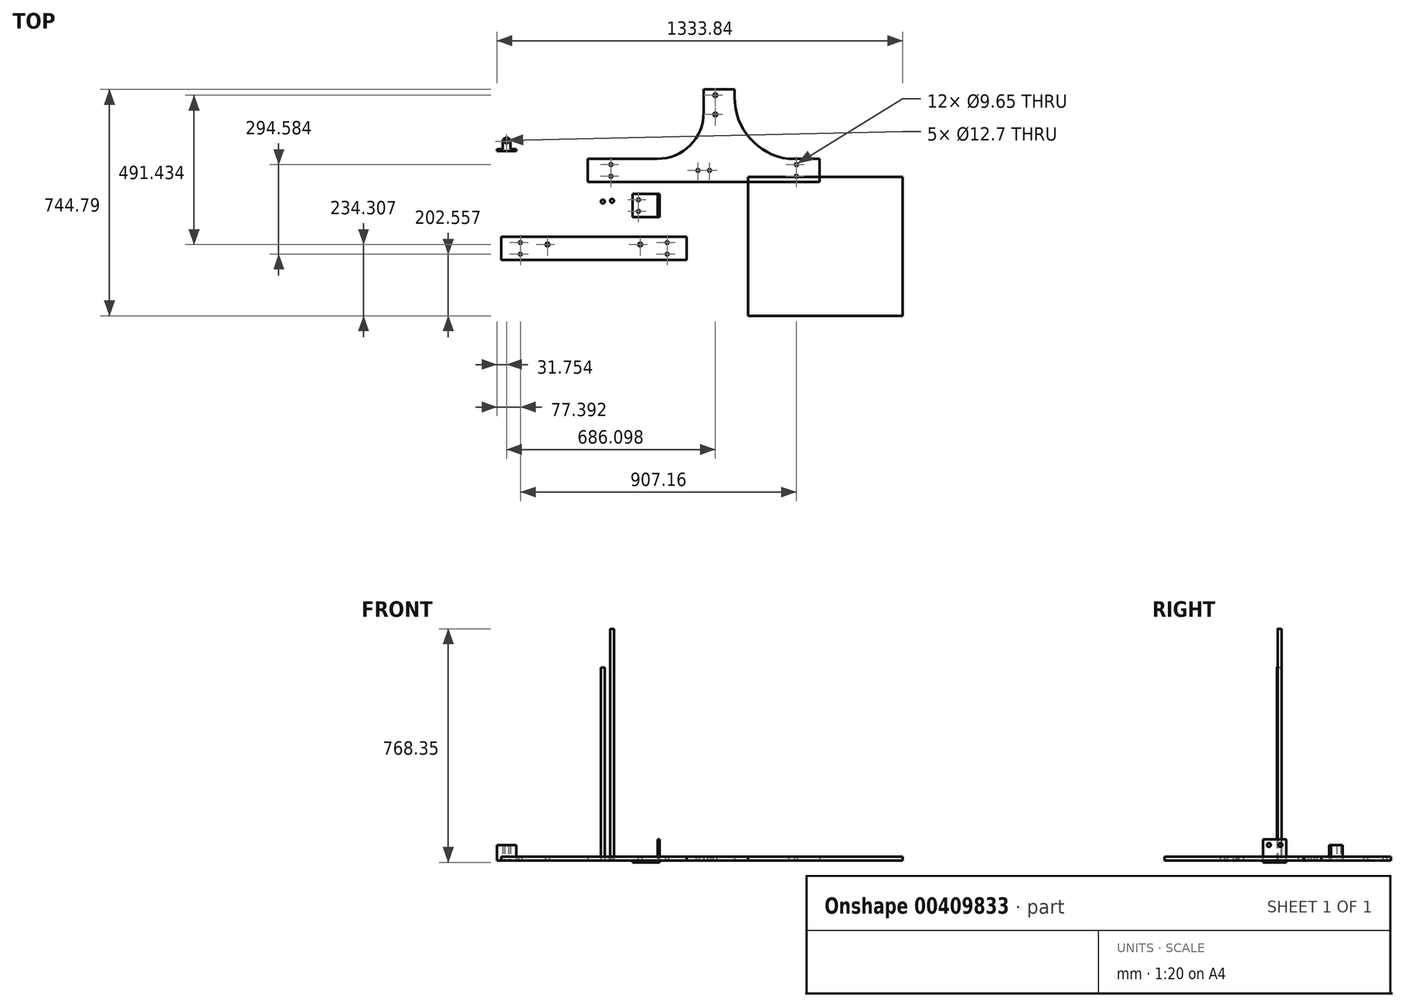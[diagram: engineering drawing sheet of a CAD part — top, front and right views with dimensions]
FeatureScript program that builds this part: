
annotation { "Feature Type Name" : "Feature", "Feature Type Description" : "" }
export const myFeature = defineFeature(function(context is Context, id is Id, definition is map)
    precondition{}
    {
        {
            var Q0;
            Q0=qCreatedBy(makeId("Top.planeOp"),FACE);
            var sketch = newSketch(context, id + "F0", { "sketchPlane" : qUnion([Q0])});
            skLineSegment(sketch, "E0.bottom", {"start": v(-396.76, -185.12) * mm, "end": v(212.84, -185.12) * mm});
            skLineSegment(sketch, "E0.top", {"start": v(-396.76, -261.32) * mm, "end": v(212.84, -261.32) * mm});
            skLineSegment(sketch, "E0.left", {"start": v(-396.76, -185.12) * mm, "end": v(-396.76, -261.32) * mm});
            skLineSegment(sketch, "E0.right", {"start": v(212.84, -185.12) * mm, "end": v(212.84, -261.32) * mm});
            skSolve(sketch);
        }
        {
            var Q0;
            Q0=makeQuery(id+"F0.imprint","IMPRINT",FACE,{"disambiguationData":[TD([[makeQuery(id+"F0.imprint","IMPRINT",EDGE,{"derivedFrom":sQuery(id+"F0.wireOp",EDGE,"E0.bottom")}),-1.0]])]});
            extrude(context, id + "F1", {"entities" : qUnion([Q0]), "depth" : 12.7 * mm});
        }
        {
            var Q0;
            Q0=qCreatedBy(makeId("Top.planeOp"),FACE);
            var sketch = newSketch(context, id + "F2", { "sketchPlane" : qUnion([Q0])});
            skLineSegment(sketch, "E1.bottom", {"start": v(-111.9, 71.36) * mm, "end": v(116.7, 71.36) * mm});
            skLineSegment(sketch, "E1.top", {"start": v(-111.9, -4.84) * mm, "end": v(650.1, -4.84) * mm});
            skLineSegment(sketch, "E1.left", {"start": v(-111.9, 71.36) * mm, "end": v(-111.9, -4.84) * mm});
            skLineSegment(sketch, "E1.right", {"start": v(650.1, 71.36) * mm, "end": v(650.1, -4.84) * mm});
            skLineSegment(sketch, "E2.top", {"start": v(269.1, 299.96) * mm, "end": v(370.7, 299.96) * mm});
            skLineSegment(sketch, "E2.left", {"start": v(269.1, 223.76) * mm, "end": v(269.1, 299.96) * mm});
            skLineSegment(sketch, "E2.right", {"start": v(370.7, 274.56) * mm, "end": v(370.7, 299.96) * mm});
            skLineSegment(sketch, "E3.trimOffspring", {"start": v(548.5, 71.36) * mm, "end": v(650.1, 71.36) * mm});
            skArc(sketch, "E4", {"start": v(116.7, 71.36) * mm, "mid": v(224.47, 116) * mm, "end": v(269.1, 223.76) * mm});
            skArc(sketch, "E5", {"start": v(370.7, 274.56) * mm, "mid": v(420.97, 139.16) * mm, "end": v(548.5, 71.36) * mm});
            skPoint(sketch, "E6.orphan", {"position": v(269.1, 71.36) * mm});
            skSolve(sketch);
        }
        {
            var Q0;
            Q0=makeQuery(id+"F2.imprint","IMPRINT",FACE,{"disambiguationData":[TD([[makeQuery(id+"F2.imprint","IMPRINT",EDGE,{"derivedFrom":sQuery(id+"F2.wireOp",EDGE,"E1.bottom")}),-1.0]])]});
            extrude(context, id + "F3", {"entities" : qUnion([Q0]), "depth" : 12.7 * mm});
        }
        {
            var Q0;
            Q0=makeQuery(id+"F1.opExtrude","CAP_FACE",FACE,{"disambiguationData":[OSD([sQuery(id+"F0.wireOp",EDGE,"E0.bottom"),sQuery(id+"F0.wireOp",EDGE,"E0.top"),sQuery(id+"F0.wireOp",EDGE,"E0.left"),sQuery(id+"F0.wireOp",EDGE,"E0.right")])],"isStart":false});
            var sketch = newSketch(context, id + "F4", { "sketchPlane" : qUnion([Q0])});
            skLineSegment(sketch, "E7", {"start": v(212.84, -223.22) * mm, "end": v(149.34, -223.22) * mm});
            skLineSegment(sketch, "E8", {"start": v(149.34, -223.22) * mm, "end": v(149.34, -204.17) * mm});
            skLineSegment(sketch, "E9.1.0.0", {"start": v(187.44, -223.22) * mm, "end": v(187.44, -204.17) * mm});
            skLineSegment(sketch, "E9.direction1", {"start": v(149.34, -223.22) * mm, "end": v(187.44, -223.22) * mm, "construction": true});
            skLineSegment(sketch, "E10.MirrorCS", {"start": v(187.44, -223.22) * mm, "end": v(187.44, -242.27) * mm});
            skLineSegment(sketch, "E11.MirrorCS", {"start": v(149.34, -223.22) * mm, "end": v(149.34, -242.27) * mm});
            skPoint(sketch, "E12.end.orphan", {"position": v(-91.96, -261.32) * mm});
            skPoint(sketch, "E12.start.orphan", {"position": v(-91.96, -185.12) * mm});
            skLineSegment(sketch, "E13", {"start": v(-91.96, -261.32) * mm, "end": v(-91.96, -241.2) * mm});
            skLineSegment(sketch, "E14.MirrorCS", {"start": v(-333.26, -223.22) * mm, "end": v(-333.26, -242.27) * mm});
            skLineSegment(sketch, "E15.MirrorCS", {"start": v(-371.36, -223.22) * mm, "end": v(-371.36, -242.27) * mm});
            skLineSegment(sketch, "E16.MirrorCS", {"start": v(-371.36, -223.22) * mm, "end": v(-371.36, -204.17) * mm});
            skLineSegment(sketch, "E17.MirrorCS", {"start": v(-333.26, -223.22) * mm, "end": v(-333.26, -204.17) * mm});
            skLineSegment(sketch, "E18", {"start": v(-91.96, -185.12) * mm, "end": v(-244.36, -185.12) * mm});
            skLineSegment(sketch, "E19", {"start": v(-91.96, -185.12) * mm, "end": v(60.44, -185.12) * mm});
            skLineSegment(sketch, "E20", {"start": v(-244.36, -185.12) * mm, "end": v(-244.36, -210.52) * mm});
            skLineSegment(sketch, "E21", {"start": v(60.44, -185.12) * mm, "end": v(60.44, -210.52) * mm});
            skSolve(sketch);
        }
        {
            var Q0;
            Q0=sQuery(id+"F4.wireOp",VERTEX,"E11.MirrorCS.end");
            var Q1;
            Q1=sQuery(id+"F4.wireOp",VERTEX,"E8.end");
            var Q2;
            Q2=sQuery(id+"F4.wireOp",VERTEX,"9953c66d-f5c9-40e7-a042-aea70b481f3b0.MirrorCS.end");
            var Q3;
            Q3=sQuery(id+"F4.wireOp",VERTEX,"f008637d-56cd-4cf4-9467-72500eb1184e0.MirrorCS.end");
            var Q4;
            Q4=sQuery(id+"F4.wireOp",VERTEX,"bad4df71-79ab-45ec-aa86-1bffc069c0d70.MirrorCS.end");
            var Q5;
            Q5=sQuery(id+"F4.wireOp",VERTEX,"125a2959-b819-4b87-9607-182dddcc34e20.MirrorCS.end");
            var Q6;
            Q6=makeQuery(id+"F1.opExtrude","SWEPT_BODY",BODY,{"disambiguationData":[OSD([sQuery(id+"F0.wireOp",EDGE,"E0.bottom"),sQuery(id+"F0.wireOp",EDGE,"E0.top"),sQuery(id+"F0.wireOp",EDGE,"E0.left"),sQuery(id+"F0.wireOp",EDGE,"E0.right")])]});
            hole(context, id + "F5", {"style" : HoleStyle.SIMPLE, "endStyle" : HoleEndStyle.BLIND, "holeDiameter" : 9.65 * mm, "holeDepth" : 25.4 * mm, "isTappedThrough" : true, "tappedDepth" : 12.7 * mm, "tapClearance" : 3, "locations" : qUnion([Q0, Q1, Q2, Q3, Q4, Q5]), "scope" : qUnion([Q6])});
        }
        {
            var Q0;
            Q0=makeQuery(id+"F3.opExtrude","CAP_FACE",FACE,{"disambiguationData":[OSD([sQuery(id+"F2.wireOp",EDGE,"E1.bottom"),sQuery(id+"F2.wireOp",EDGE,"E1.top"),sQuery(id+"F2.wireOp",EDGE,"E1.left"),sQuery(id+"F2.wireOp",EDGE,"E1.right"),sQuery(id+"F2.wireOp",EDGE,"E2.top"),sQuery(id+"F2.wireOp",EDGE,"E2.left"),sQuery(id+"F2.wireOp",EDGE,"E2.right"),sQuery(id+"F2.wireOp",EDGE,"E3.trimOffspring"),sQuery(id+"F2.wireOp",EDGE,"E4"),sQuery(id+"F2.wireOp",EDGE,"E5")])],"isStart":false});
            var sketch = newSketch(context, id + "F6", { "sketchPlane" : qUnion([Q0])});
            skLineSegment(sketch, "E22", {"start": v(-111.9, 33.26) * mm, "end": v(-35.7, 33.26) * mm});
            skLineSegment(sketch, "E23", {"start": v(-35.7, 33.26) * mm, "end": v(-35.7, 14.21) * mm});
            skLineSegment(sketch, "E24", {"start": v(-35.7, 14.21) * mm, "end": v(-73.8, 14.21) * mm});
            skLineSegment(sketch, "E25.MirrorCS", {"start": v(-35.7, 52.31) * mm, "end": v(-73.8, 52.31) * mm});
            skLineSegment(sketch, "E26", {"start": v(269.1, -4.84) * mm, "end": v(269.1, 15.48) * mm});
            skLineSegment(sketch, "E27.MirrorCS", {"start": v(573.9, 14.21) * mm, "end": v(612, 14.21) * mm});
            skLineSegment(sketch, "E28.MirrorCS", {"start": v(573.9, 52.31) * mm, "end": v(612, 52.31) * mm});
            skSolve(sketch);
        }
        {
            var Q0;
            Q0=sQuery(id+"F6.wireOp",VERTEX,"E25.MirrorCS.start");
            var Q1;
            Q1=sQuery(id+"F6.wireOp",VERTEX,"E24.start");
            var Q2;
            Q2=sQuery(id+"F6.wireOp",VERTEX,"E28.MirrorCS.start");
            var Q3;
            Q3=sQuery(id+"F6.wireOp",VERTEX,"E27.MirrorCS.start");
            var Q4;
            Q4=makeQuery(id+"F3.opExtrude","SWEPT_BODY",BODY,{"disambiguationData":[OSD([sQuery(id+"F2.wireOp",EDGE,"E1.bottom"),sQuery(id+"F2.wireOp",EDGE,"E1.top"),sQuery(id+"F2.wireOp",EDGE,"E1.left"),sQuery(id+"F2.wireOp",EDGE,"E1.right"),sQuery(id+"F2.wireOp",EDGE,"E2.top"),sQuery(id+"F2.wireOp",EDGE,"E2.left"),sQuery(id+"F2.wireOp",EDGE,"E2.right"),sQuery(id+"F2.wireOp",EDGE,"E3.trimOffspring"),sQuery(id+"F2.wireOp",EDGE,"E4"),sQuery(id+"F2.wireOp",EDGE,"E5")])]});
            hole(context, id + "F7", {"style" : HoleStyle.SIMPLE, "endStyle" : HoleEndStyle.BLIND, "holeDiameter" : 9.65 * mm, "holeDepth" : 25.4 * mm, "isTappedThrough" : true, "tappedDepth" : 12.7 * mm, "tapClearance" : 3, "locations" : qUnion([Q0, Q1, Q2, Q3]), "scope" : qUnion([Q4])});
        }
        {
            var Q0;
            Q0=sQuery(id+"F4.wireOp",VERTEX,"E17.MirrorCS.end");
            var Q1;
            Q1=sQuery(id+"F4.wireOp",VERTEX,"E14.MirrorCS.end");
            var Q2;
            Q2=makeQuery(id+"F1.opExtrude","SWEPT_BODY",BODY,{"disambiguationData":[OSD([sQuery(id+"F0.wireOp",EDGE,"E0.bottom"),sQuery(id+"F0.wireOp",EDGE,"E0.top"),sQuery(id+"F0.wireOp",EDGE,"E0.left"),sQuery(id+"F0.wireOp",EDGE,"E0.right")])]});
            hole(context, id + "F8", {"style" : HoleStyle.SIMPLE, "endStyle" : HoleEndStyle.BLIND, "holeDiameter" : 9.65 * mm, "holeDepth" : 25.4 * mm, "isTappedThrough" : true, "tappedDepth" : 12.7 * mm, "tapClearance" : 3, "locations" : qUnion([Q0, Q1]), "scope" : qUnion([Q2])});
        }
        {
            var Q0;
            Q0=makeQuery(id+"F3.opExtrude","CAP_FACE",FACE,{"disambiguationData":[OSD([sQuery(id+"F2.wireOp",EDGE,"E1.bottom"),sQuery(id+"F2.wireOp",EDGE,"E1.top"),sQuery(id+"F2.wireOp",EDGE,"E1.left"),sQuery(id+"F2.wireOp",EDGE,"E1.right"),sQuery(id+"F2.wireOp",EDGE,"E2.top"),sQuery(id+"F2.wireOp",EDGE,"E2.left"),sQuery(id+"F2.wireOp",EDGE,"E2.right"),sQuery(id+"F2.wireOp",EDGE,"E3.trimOffspring"),sQuery(id+"F2.wireOp",EDGE,"E4"),sQuery(id+"F2.wireOp",EDGE,"E5")])],"isStart":false});
            var sketch = newSketch(context, id + "F9", { "sketchPlane" : qUnion([Q0])});
            skLineSegment(sketch, "E29", {"start": v(269.1, -4.84) * mm, "end": v(269.1, 33.26) * mm});
            skLineSegment(sketch, "E30", {"start": v(269.1, 33.26) * mm, "end": v(288.15, 33.26) * mm});
            skLineSegment(sketch, "E31", {"start": v(269.1, 33.26) * mm, "end": v(250.05, 33.26) * mm});
            skSolve(sketch);
        }
        {
            var Q0;
            Q0=sQuery(id+"F9.wireOp",VERTEX,"E30.end");
            var Q1;
            Q1=sQuery(id+"F9.wireOp",VERTEX,"E31.end");
            var Q2;
            Q2=makeQuery(id+"F3.opExtrude","SWEPT_BODY",BODY,{"disambiguationData":[OSD([sQuery(id+"F2.wireOp",EDGE,"E1.bottom"),sQuery(id+"F2.wireOp",EDGE,"E1.top"),sQuery(id+"F2.wireOp",EDGE,"E1.left"),sQuery(id+"F2.wireOp",EDGE,"E1.right"),sQuery(id+"F2.wireOp",EDGE,"E2.top"),sQuery(id+"F2.wireOp",EDGE,"E2.left"),sQuery(id+"F2.wireOp",EDGE,"E2.right"),sQuery(id+"F2.wireOp",EDGE,"E3.trimOffspring"),sQuery(id+"F2.wireOp",EDGE,"E4"),sQuery(id+"F2.wireOp",EDGE,"E5")])]});
            hole(context, id + "F10", {"style" : HoleStyle.SIMPLE, "endStyle" : HoleEndStyle.BLIND, "holeDiameter" : 9.65 * mm, "holeDepth" : 25.4 * mm, "isTappedThrough" : true, "tappedDepth" : 12.7 * mm, "tapClearance" : 3, "locations" : qUnion([Q0, Q1]), "scope" : qUnion([Q2])});
        }
        {
            var Q0;
            Q0=makeQuery(id+"F3.opExtrude","CAP_FACE",FACE,{"disambiguationData":[OSD([sQuery(id+"F2.wireOp",EDGE,"E1.bottom"),sQuery(id+"F2.wireOp",EDGE,"E1.top"),sQuery(id+"F2.wireOp",EDGE,"E1.left"),sQuery(id+"F2.wireOp",EDGE,"E1.right"),sQuery(id+"F2.wireOp",EDGE,"E2.top"),sQuery(id+"F2.wireOp",EDGE,"E2.left"),sQuery(id+"F2.wireOp",EDGE,"E2.right"),sQuery(id+"F2.wireOp",EDGE,"E3.trimOffspring"),sQuery(id+"F2.wireOp",EDGE,"E4"),sQuery(id+"F2.wireOp",EDGE,"E5")])],"isStart":false});
            var sketch = newSketch(context, id + "F11", { "sketchPlane" : qUnion([Q0])});
            skLineSegment(sketch, "E32", {"start": v(307.2, 280.91) * mm, "end": v(307.2, 217.41) * mm});
            skPoint(sketch, "E33.start.orphan", {"position": v(319.9, 299.96) * mm});
            skSolve(sketch);
        }
        {
            var Q0;
            Q0=sQuery(id+"F11.wireOp",VERTEX,"E33.end");
            var Q1;
            Q1=sQuery(id+"F11.wireOp",VERTEX,"E32.end");
            var Q2;
            Q2=makeQuery(id+"F3.opExtrude","SWEPT_BODY",BODY,{"disambiguationData":[OSD([sQuery(id+"F2.wireOp",EDGE,"E1.bottom"),sQuery(id+"F2.wireOp",EDGE,"E1.top"),sQuery(id+"F2.wireOp",EDGE,"E1.left"),sQuery(id+"F2.wireOp",EDGE,"E1.right"),sQuery(id+"F2.wireOp",EDGE,"E2.top"),sQuery(id+"F2.wireOp",EDGE,"E2.left"),sQuery(id+"F2.wireOp",EDGE,"E2.right"),sQuery(id+"F2.wireOp",EDGE,"E3.trimOffspring"),sQuery(id+"F2.wireOp",EDGE,"E4"),sQuery(id+"F2.wireOp",EDGE,"E5")])]});
            hole(context, id + "F12", {"style" : HoleStyle.SIMPLE, "endStyle" : HoleEndStyle.BLIND, "holeDiameter" : 12.7 * mm, "holeDepth" : 25.4 * mm, "isTappedThrough" : true, "tappedDepth" : 12.7 * mm, "tapClearance" : 3, "locations" : qUnion([Q0, Q1]), "scope" : qUnion([Q2])});
        }
        {
            var Q0;
            Q0=qCreatedBy(makeId("Top.planeOp"),FACE);
            var sketch = newSketch(context, id + "F13", { "sketchPlane" : qUnion([Q0])});
            skCircle(sketch, "E34", {"center": v(-62.58, -69.02) * mm, "radius": 6.35 * mm});
            skSolve(sketch);
        }
        {
            var Q0;
            Q0 = qSketchRegion(id + "F13", true);
            extrude(context, id + "F14", {"entities" : qUnion([Q0]), "depth" : 635 * mm});
        }
        {
            var Q0;
            Q0=sQuery(id+"F4.wireOp",VERTEX,"E20.end");
            var Q1;
            Q1=sQuery(id+"F4.wireOp",VERTEX,"E21.end");
            var Q2;
            Q2=makeQuery(id+"F1.opExtrude","SWEPT_BODY",BODY,{"disambiguationData":[OSD([sQuery(id+"F0.wireOp",EDGE,"E0.bottom"),sQuery(id+"F0.wireOp",EDGE,"E0.top"),sQuery(id+"F0.wireOp",EDGE,"E0.left"),sQuery(id+"F0.wireOp",EDGE,"E0.right")])]});
            hole(context, id + "F15", {"style" : HoleStyle.SIMPLE, "endStyle" : HoleEndStyle.BLIND, "holeDiameter" : 12.7 * mm, "holeDepth" : 25.4 * mm, "isTappedThrough" : true, "tappedDepth" : 12.7 * mm, "tapClearance" : 3, "locations" : qUnion([Q0, Q1]), "scope" : qUnion([Q2])});
        }
        {
            var Q0;
            Q0=qCreatedBy(makeId("Top.planeOp"),FACE);
            var sketch = newSketch(context, id + "F16", { "sketchPlane" : qUnion([Q0])});
            skCircle(sketch, "E35", {"center": v(-32.14, -66.79) * mm, "radius": 6.35 * mm});
            skSolve(sketch);
        }
        {
            var Q0;
            Q0 = qSketchRegion(id + "F16", true);
            extrude(context, id + "F17", {"entities" : qUnion([Q0]), "depth" : 762 * mm});
        }
        {
            var Q0;
            Q0=qCreatedBy(makeId("Top.planeOp"),FACE);
            var sketch = newSketch(context, id + "F18", { "sketchPlane" : qUnion([Q0])});
            skLineSegment(sketch, "E36.bottom", {"start": v(48.39, -44.35) * mm, "end": v(124.59, -44.35) * mm});
            skLineSegment(sketch, "E36.top", {"start": v(48.39, -120.55) * mm, "end": v(124.59, -120.55) * mm});
            skLineSegment(sketch, "E36.left", {"start": v(48.39, -44.35) * mm, "end": v(48.39, -120.55) * mm});
            skLineSegment(sketch, "E36.right", {"start": v(124.59, -44.35) * mm, "end": v(124.59, -120.55) * mm});
            skPoint(sketch, "E37.middle", {"position": v(86.49, -82.45) * mm});
            skPoint(sketch, "E38.orphan", {"position": v(105.54, -101.5) * mm});
            skPoint(sketch, "E37.right.end.orphan", {"position": v(67.44, -101.5) * mm});
            skPoint(sketch, "E37.bottom.start.orphan", {"position": v(105.54, -63.4) * mm});
            skPoint(sketch, "E39.end.orphan", {"position": v(67.44, -63.4) * mm});
            skLineSegment(sketch, "E40", {"start": v(124.59, -44.35) * mm, "end": v(118.24, -44.35) * mm, "construction": true});
            skLineSegment(sketch, "E41", {"start": v(118.24, -44.35) * mm, "end": v(118.24, -120.55) * mm});
            skSolve(sketch);
        }
        {
            var Q0;
            Q0 = qSketchRegion(id + "F18", true);
            var Q1;
            {var subQ2=sQuery(id+"F18.wireOp",EDGE,"E37.top");Q1=makeQuery(id+"F18.imprint","IMPRINT",FACE,{"disambiguationData":[TD([[makeQuery(id+"F18.imprint","IMPRINT",EDGE,{"derivedFrom":subQ2}),-1.0]])]});}
            var Q2;
            {var subQ0=sQuery(id+"F18.wireOp",EDGE,"E37.bottom");Q2=makeQuery(id+"F18.imprint","IMPRINT",FACE,{"disambiguationData":[TD([[makeQuery(id+"F18.imprint","IMPRINT",EDGE,{"derivedFrom":subQ0}),1.0]])]});}
            extrude(context, id + "F19", {"entities" : qUnion([Q0, Q1, Q2]), "oppositeDirection" : true, "depth" : 6.35 * mm});
        }
        {
            var Q0;
            {var subQ0=sQuery(id+"F18.wireOp",EDGE,"E36.right");Q0=makeQuery(id+"F18.imprint","IMPRINT",FACE,{"disambiguationData":[TD([[makeQuery(id+"F18.imprint","IMPRINT",EDGE,{"derivedFrom":subQ0}),-1.0]])]});}
            extrude(context, id + "F20", {"entities" : qUnion([Q0]), "operationType" : NewBodyOperationType.ADD, "depth" : 69.85 * mm});
        }
        {
            var Q0;
            {var subQ0=sQuery(id+"F18.wireOp",EDGE,"E36.right");Q0=makeQuery(id+"F20.boolean.opBoolean","MERGE",FACE,{"derivedFrom":[makeQuery(id+"F19.opExtrude","SWEPT_FACE",FACE,{"disambiguationData":[OSD([subQ0])]}),makeQuery(id+"F20.opExtrude","SWEPT_FACE",FACE,{"disambiguationData":[OSD([subQ0])]})]});}
            var sketch = newSketch(context, id + "F21", { "sketchPlane" : qUnion([Q0])});
            skPoint(sketch, "E42.middle", {"position": v(-82.45, 31.75) * mm});
            skPoint(sketch, "E42.bottom.start.orphan", {"position": v(-63.4, 50.8) * mm});
            skPoint(sketch, "E42.right.start.orphan", {"position": v(-101.5, 50.8) * mm});
            skPoint(sketch, "E42.top.end.orphan", {"position": v(-101.5, 12.7) * mm});
            skPoint(sketch, "E42.top.start.orphan", {"position": v(-63.4, 12.7) * mm});
            skPoint(sketch, "E43.trimOffspring.end.orphan", {"position": v(-44.35, -6.35) * mm});
            skPoint(sketch, "E44.start.orphan", {"position": v(-120.55, 69.85) * mm});
            skSolve(sketch);
        }
        {
            var Q0;
            Q0=sQuery(id+"F21.wireOp",VERTEX,"E42.right.start.orphan");
            var Q1;
            Q1=sQuery(id+"F21.wireOp",VERTEX,"E42.bottom.start.orphan");
            var Q2;
            Q2=makeQuery(id+"F19.opExtrude","SWEPT_BODY",BODY,{"disambiguationData":[OSD([sQuery(id+"F18.wireOp",EDGE,"E36.bottom"),sQuery(id+"F18.wireOp",EDGE,"E36.top"),sQuery(id+"F18.wireOp",EDGE,"E36.left"),sQuery(id+"F18.wireOp",EDGE,"E36.right")])]});
            hole(context, id + "F22", {"style" : HoleStyle.SIMPLE, "endStyle" : HoleEndStyle.BLIND, "holeDiameter" : 12.7 * mm, "holeDepth" : 25.4 * mm, "isTappedThrough" : true, "tappedDepth" : 12.7 * mm, "tapClearance" : 3, "locations" : qUnion([Q0, Q1]), "scope" : qUnion([Q2])});
        }
        {
            var Q0;
            Q0=sQuery(id+"F11.wireOp",VERTEX,"E32.start");
            var Q1;
            Q1=makeQuery(id+"F3.opExtrude","SWEPT_BODY",BODY,{"disambiguationData":[OSD([sQuery(id+"F2.wireOp",EDGE,"E1.bottom"),sQuery(id+"F2.wireOp",EDGE,"E1.top"),sQuery(id+"F2.wireOp",EDGE,"E1.left"),sQuery(id+"F2.wireOp",EDGE,"E1.right"),sQuery(id+"F2.wireOp",EDGE,"E2.top"),sQuery(id+"F2.wireOp",EDGE,"E2.left"),sQuery(id+"F2.wireOp",EDGE,"E2.right"),sQuery(id+"F2.wireOp",EDGE,"E3.trimOffspring"),sQuery(id+"F2.wireOp",EDGE,"E4"),sQuery(id+"F2.wireOp",EDGE,"E5")])]});
            hole(context, id + "F23", {"style" : HoleStyle.SIMPLE, "endStyle" : HoleEndStyle.BLIND, "holeDiameter" : 12.7 * mm, "holeDepth" : 25.4 * mm, "isTappedThrough" : true, "tappedDepth" : 12.7 * mm, "tapClearance" : 3, "locations" : qUnion([Q0]), "scope" : qUnion([Q1])});
        }
        {
            var Q0;
            Q0=qCreatedBy(makeId("Top.planeOp"),FACE);
            var sketch = newSketch(context, id + "F24", { "sketchPlane" : qUnion([Q0])});
            skLineSegment(sketch, "E45.bottom", {"start": v(415.19, 12.37) * mm, "end": v(923.19, 12.37) * mm});
            skLineSegment(sketch, "E45.top", {"start": v(415.19, -444.83) * mm, "end": v(923.19, -444.83) * mm});
            skLineSegment(sketch, "E45.left", {"start": v(415.19, 12.37) * mm, "end": v(415.19, -444.83) * mm});
            skLineSegment(sketch, "E45.right", {"start": v(923.19, 12.37) * mm, "end": v(923.19, -444.83) * mm});
            skSolve(sketch);
        }
        {
            var Q0;
            Q0 = qSketchRegion(id + "F24", true);
            extrude(context, id + "F25", {"entities" : qUnion([Q0]), "depth" : 12.7 * mm});
        }
        {
            var Q0;
            Q0=qCreatedBy(makeId("Top.planeOp"),FACE);
            var sketch = newSketch(context, id + "F26", { "sketchPlane" : qUnion([Q0])});
            skLineSegment(sketch, "E46", {"start": v(-410.65, 96.62) * mm, "end": v(-347.15, 96.62) * mm});
            skLineSegment(sketch, "E47", {"start": v(-347.15, 96.62) * mm, "end": v(-347.15, 102.97) * mm});
            skLineSegment(sketch, "E48", {"start": v(-347.15, 102.97) * mm, "end": v(-366.2, 102.97) * mm});
            skLineSegment(sketch, "E49", {"start": v(-366.2, 102.97) * mm, "end": v(-366.2, 128.37) * mm});
            skLineSegment(sketch, "E50", {"start": v(-378.9, 141.07) * mm, "end": v(-378.9, 141.07) * mm});
            skLineSegment(sketch, "E51", {"start": v(-391.6, 128.37) * mm, "end": v(-391.6, 102.97) * mm});
            skLineSegment(sketch, "E52", {"start": v(-391.6, 102.97) * mm, "end": v(-410.65, 102.97) * mm});
            skLineSegment(sketch, "E53", {"start": v(-410.65, 102.97) * mm, "end": v(-410.65, 96.62) * mm});
            skPoint(sketch, "E54.visualSharp", {"position": v(-391.6, 141.07) * mm});
            skArc(sketch, "E54.filletArc", {"start": v(-378.9, 141.07) * mm, "mid": v(-387.88, 137.35) * mm, "end": v(-391.6, 128.37) * mm});
            skPoint(sketch, "E55.visualSharp", {"position": v(-366.2, 141.07) * mm});
            skArc(sketch, "E55.filletArc", {"start": v(-366.2, 128.37) * mm, "mid": v(-369.92, 137.35) * mm, "end": v(-378.9, 141.07) * mm});
            skCircle(sketch, "E56", {"center": v(-378.9, 128.37) * mm, "radius": 6.35 * mm});
            skSolve(sketch);
        }
        {
            var Q0;
            Q0 = qSketchRegion(id + "F26", true);
            extrude(context, id + "F27", {"entities" : qUnion([Q0]), "depth" : 50.8 * mm});
        }
        {
            var Q0;
            Q0=makeQuery(id+"F19.opExtrude","SWEPT_FACE",FACE,{"disambiguationData":[OSD([sQuery(id+"F18.wireOp",EDGE,"E36.left")])]});
            extrude(context, id + "F28", {"entities" : qUnion([Q0]), "operationType" : NewBodyOperationType.ADD, "depth" : 12.7 * mm});
        }
        {
            var Q0;
            {var subQ0=sQuery(id+"F18.wireOp",EDGE,"E36.left");Q0=makeQuery(id+"F28.boolean.opBoolean","MERGE",FACE,{"derivedFrom":[makeQuery(id+"F19.opExtrude","CAP_FACE",FACE,{"disambiguationData":[OSD([sQuery(id+"F18.wireOp",EDGE,"E36.bottom"),sQuery(id+"F18.wireOp",EDGE,"E36.top"),subQ0,sQuery(id+"F18.wireOp",EDGE,"E36.right")])],"isStart":true}),makeQuery(id+"F28.opExtrude","SWEPT_FACE",FACE,{"disambiguationData":[OSD([subQ0]),TDD([makeQuery(id+"F19.opExtrude","CAP_EDGE",EDGE,{"disambiguationData":[OSD([subQ0])],"isStart":true})])]})]});}
            var sketch = newSketch(context, id + "F29", { "sketchPlane" : qUnion([Q0])});
            skLineSegment(sketch, "E57", {"start": v(35.69, -82.45) * mm, "end": v(54.74, -82.45) * mm});
            skLineSegment(sketch, "E58", {"start": v(54.74, -82.45) * mm, "end": v(54.74, -63.4) * mm});
            skLineSegment(sketch, "E59", {"start": v(54.74, -82.45) * mm, "end": v(54.74, -101.5) * mm});
            skSolve(sketch);
        }
        {
            var Q0;
            Q0=sQuery(id+"F29.wireOp",VERTEX,"E58.end");
            var Q1;
            Q1=sQuery(id+"F29.wireOp",VERTEX,"E59.end");
            var Q2;
            Q2=makeQuery(id+"F19.opExtrude","SWEPT_BODY",BODY,{"disambiguationData":[OSD([sQuery(id+"F18.wireOp",EDGE,"E36.bottom"),sQuery(id+"F18.wireOp",EDGE,"E36.top"),sQuery(id+"F18.wireOp",EDGE,"E36.left"),sQuery(id+"F18.wireOp",EDGE,"E36.right")])]});
            hole(context, id + "F30", {"style" : HoleStyle.SIMPLE, "endStyle" : HoleEndStyle.BLIND, "holeDiameter" : 9.65 * mm, "holeDepth" : 25.4 * mm, "isTappedThrough" : true, "tappedDepth" : 12.7 * mm, "tapClearance" : 3, "locations" : qUnion([Q0, Q1]), "scope" : qUnion([Q2])});
        }
    });
